# Revit family: IS_Connect2_K9578_BIM_GB
name_source: partatom
category: Plumbing Fixtures
revit_build: Autodesk Revit 2017 (Build: 20160225_1515(x64)
units: mm (PartAtom-declared; Revit-internal decimal feet)

## family parameters
Always vertical = No
Cut with Voids When Loaded = No
OmniClass Number = 23.45.05.14.21.11
OmniClass Title = Bath/Shower Units
Part Type = Normal
Room Calculation Point = No
Round Connector Dimension = Use Diameter
Shared = No
Work Plane-Based = No

## types (1)
- K9578EO - UK 1000 SIDE PANEL – LH INSTALLATION
    Accessories = www.idealspec.co.uk
    AreaUnits = millimeters
    AssetType = Fixed
    BIMObjectName = ISI_IdealStandard_ShowersEnclosures_ConnectII_K9578EO
    Brand = Ideal Standard
    CisternCapacity = 0 m³
    Color = Silver, clear
    CurrencyUnit = £
    Description = CONNECT 2 SHOWER ENCLOSURE SIDE PANEL  CLEAR 6 MM CLEAR SAFETY GLASS WITH IDEAL CLEAN TREATMENT, and BRIGHT SILVER FINISH.
    DurationUnit = year
    ExpectedLife = 30
    Features = SHOWER ENCLOSURE SIDE PANEL  CLEAR 6 MM CLEAR SAFETY GLASS WITH IDEAL CLEAN TREATMENT, and BRIGHT SILVER FINISH.
    Finish = Clear, silver
    FlushRate = 0 m³
    FlushingRate = 0
    HasGrabHandles = No
    HasIntegralShutOffDevice = No
    HasTray = No
    IfcExportAs = IfcFurnitureType
    IfcExportType = USERDEFINED
    InletConnectionSize = 0 mm  [stored 0 ft]
    Installation instructions = https://www.idealspec.co.uk
    InstallationInstructions = www.idealspec.co.uk/resources.html
    IsAutomaticFlush = No
    IsBuiltIn = No
    IsHighPressure = No
    IsSingleFlush = No
    LinearUnits = millimeters
    MainColor = Silver, clear
    ManufacturerURL = www.idealspec.co.uk
    Material = Glass
    MaterialThickness = 0 mm  [stored 0 ft]
    Model = K9578EO
    ModelNumber = K9578EO
    ModelReference = CONNECT 2 SHOWER ENCLOSURE SIDE PANEL  CLEAR 6 MM CLEAR SAFETY GLASS WITH IDEAL CLEAN TREATMENT, and BRIGHT SILVER FINISH.
    Name = ShowerEnclosure_CONNECT-2K9578EO_IdealStandard
    NominalHeight = 1953 mm  [stored 6.40748 ft]
    NominalLength = 955 mm
    NominalWidth = 46 mm
    OutletConnectionSize = 0 mm  [stored 0 ft]
    Product certification = https://www.idealspec.co.uk
    Product group = Shower Enclosure
    ProductInformation = www.idealspec.co.uk/datasheets/K9578EO
    SeatHasCover = No
    Shape = Rectangular
    Size = 1953 x 955 x 46mm
    Space = Internal
    SpareParts = www.fastpart-spares.co.uk
    SpilloverLevel = 0 mm  [stored 0 ft]
    URL = www.idealspec.co.uk
    Uniclass 2015 Code = Pr_40_20_93_94
    Uniclass 2015 Name = WC pans
    Uniclass2015Code = Pr_40_20_06_79
    Uniclass2015Title = Shower enclosures
    Uniclass2015Version = v1.15
    Version = 1
    VolumeUnits = Litres
    WarrantyDescription = Manufacturers warranty
    WarrantyDurationUnit = year

note: [stored X ft] marks values corroborated as IEEE doubles in the binary element streams (Revit-internal decimal feet)

## geometry (parser evidence)
native form markers: Sweep x2
no freeform markers — native parametric forms only
